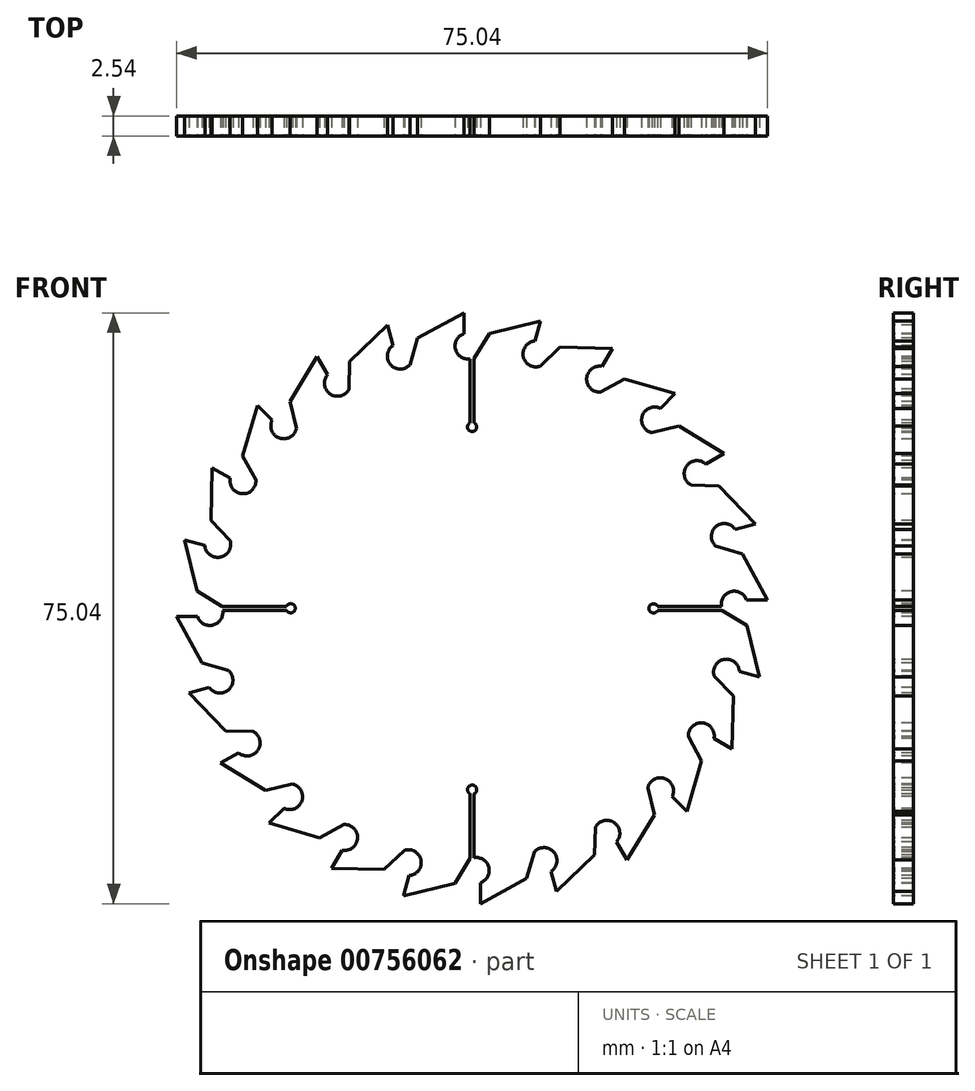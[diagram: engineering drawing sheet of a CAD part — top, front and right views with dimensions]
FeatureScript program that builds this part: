
annotation { "Feature Type Name" : "Feature", "Feature Type Description" : "" }
export const myFeature = defineFeature(function(context is Context, id is Id, definition is map)
    precondition{}
    {
        {
            var Q0;
            Q0=qCreatedBy(makeId("Front.planeOp"),FACE);
            var sketch = newSketch(context, id + "F0", { "sketchPlane" : qUnion([Q0])});
            skCircle(sketch, "E0", {"center": v(0, 0) * mm, "radius": 38.1 * mm});
            skSolve(sketch);
        }
        {
            var Q0;
            Q0 = qSketchRegion(id + "F0", true);
            extrude(context, id + "F1", {"entities" : qUnion([Q0]), "endBound" : BoundingType.SYMMETRIC, "depth" : 2.54 * mm, "offsetDistance" : 25.4 * mm});
        }
        {
            var Q0;
            Q0=makeQuery(id+"F1.opExtrude","CAP_FACE",FACE,{"disambiguationData":[OSD([sQuery(id+"F0.wireOp",EDGE,"E0")])],"isStart":false});
            var sketch = newSketch(context, id + "F2", { "sketchPlane" : qUnion([Q0])});
            skArc(sketch, "E1", {"start": v(-36.8, 9.88) * mm, "mid": v(-37.84, 4.46) * mm, "end": v(-38.09, -1.05) * mm});
            skLineSegment(sketch, "E2.bottom", {"start": v(-23.57, 0.25) * mm, "end": v(-31.75, 0.25) * mm});
            skLineSegment(sketch, "E2.top", {"start": v(-23.57, -0.25) * mm, "end": v(-31.69, -0.25) * mm});
            skArc(sketch, "E3", {"start": v(-23.57, -0.25) * mm, "mid": v(-22.46, 0) * mm, "end": v(-23.57, 0.25) * mm});
            skArc(sketch, "E4", {"start": v(-34.87, -1.05) * mm, "mid": v(-32.9, -2.12) * mm, "end": v(-31.69, -0.25) * mm});
            skLineSegment(sketch, "E5", {"start": v(-34.87, -1.05) * mm, "end": v(-38.09, -1.05) * mm});
            skLineSegment(sketch, "E6", {"start": v(-31.75, 0.25) * mm, "end": v(-34.93, 2.2) * mm});
            skLineSegment(sketch, "E7", {"start": v(-34.93, 2.2) * mm, "end": v(-36.8, 9.88) * mm});
            skLineSegment(sketch, "E8.1.0", {"start": v(0.25, -23.57) * mm, "end": v(0.25, -31.69) * mm});
            skLineSegment(sketch, "E8.1.1", {"start": v(-0.25, -23.57) * mm, "end": v(-0.25, -31.75) * mm});
            skArc(sketch, "E8.1.2", {"start": v(-9.88, -36.8) * mm, "mid": v(-4.46, -37.84) * mm, "end": v(1.05, -38.09) * mm});
            skLineSegment(sketch, "E8.1.3", {"start": v(-2.2, -34.93) * mm, "end": v(-9.88, -36.8) * mm});
            skArc(sketch, "E8.1.4", {"start": v(-9.88, -36.8) * mm, "mid": v(-4.46, -37.84) * mm, "end": v(1.05, -38.09) * mm});
            skLineSegment(sketch, "E8.1.5", {"start": v(-0.25, -31.75) * mm, "end": v(-2.2, -34.93) * mm});
            skLineSegment(sketch, "E8.1.6", {"start": v(1.05, -34.87) * mm, "end": v(1.05, -38.09) * mm});
            skArc(sketch, "E8.1.7", {"start": v(1.05, -34.87) * mm, "mid": v(2.12, -32.9) * mm, "end": v(0.25, -31.69) * mm});
            skArc(sketch, "E8.1.8", {"start": v(0.25, -23.57) * mm, "mid": v(0, -22.46) * mm, "end": v(-0.25, -23.57) * mm});
            skLineSegment(sketch, "E8.2.0", {"start": v(23.57, 0.25) * mm, "end": v(31.69, 0.25) * mm});
            skLineSegment(sketch, "E8.2.1", {"start": v(23.57, -0.25) * mm, "end": v(31.75, -0.25) * mm});
            skArc(sketch, "E8.2.2", {"start": v(36.8, -9.88) * mm, "mid": v(37.84, -4.46) * mm, "end": v(38.09, 1.05) * mm});
            skLineSegment(sketch, "E8.2.3", {"start": v(34.93, -2.2) * mm, "end": v(36.8, -9.88) * mm});
            skArc(sketch, "E8.2.4", {"start": v(36.8, -9.88) * mm, "mid": v(37.84, -4.46) * mm, "end": v(38.09, 1.05) * mm});
            skLineSegment(sketch, "E8.2.5", {"start": v(31.75, -0.25) * mm, "end": v(34.93, -2.2) * mm});
            skLineSegment(sketch, "E8.2.6", {"start": v(34.87, 1.05) * mm, "end": v(38.09, 1.05) * mm});
            skArc(sketch, "E8.2.7", {"start": v(34.87, 1.05) * mm, "mid": v(32.9, 2.12) * mm, "end": v(31.69, 0.25) * mm});
            skArc(sketch, "E8.2.8", {"start": v(23.57, 0.25) * mm, "mid": v(22.46, 0) * mm, "end": v(23.57, -0.25) * mm});
            skLineSegment(sketch, "E8.3.0", {"start": v(-0.25, 23.57) * mm, "end": v(-0.25, 31.69) * mm});
            skLineSegment(sketch, "E8.3.1", {"start": v(0.25, 23.57) * mm, "end": v(0.25, 31.75) * mm});
            skArc(sketch, "E8.3.2", {"start": v(9.88, 36.8) * mm, "mid": v(4.46, 37.84) * mm, "end": v(-1.05, 38.09) * mm});
            skLineSegment(sketch, "E8.3.3", {"start": v(2.2, 34.93) * mm, "end": v(9.88, 36.8) * mm});
            skArc(sketch, "E8.3.4", {"start": v(9.88, 36.8) * mm, "mid": v(4.46, 37.84) * mm, "end": v(-1.05, 38.09) * mm});
            skLineSegment(sketch, "E8.3.5", {"start": v(0.25, 31.75) * mm, "end": v(2.2, 34.93) * mm});
            skLineSegment(sketch, "E8.3.6", {"start": v(-1.05, 34.87) * mm, "end": v(-1.05, 38.09) * mm});
            skArc(sketch, "E8.3.7", {"start": v(-1.05, 34.87) * mm, "mid": v(-2.12, 32.9) * mm, "end": v(-0.25, 31.69) * mm});
            skArc(sketch, "E8.3.8", {"start": v(-0.25, 23.57) * mm, "mid": v(0, 22.46) * mm, "end": v(0.25, 23.57) * mm});
            skSolve(sketch);
        }
        {
            var Q0;
            Q0 = qSketchRegion(id + "F2", true);
            var Q1;
            Q1=makeQuery(id+"F1.opExtrude","CAP_FACE",FACE,{"disambiguationData":[OSD([sQuery(id+"F0.wireOp",EDGE,"E0")])],"isStart":true});
            extrude(context, id + "F3", {"entities" : qUnion([Q0]), "operationType" : NewBodyOperationType.REMOVE, "endBound" : BoundingType.UP_TO_SURFACE, "oppositeDirection" : true, "depth" : 25.4 * mm, "endBoundEntityFace" : qUnion([Q1]), "offsetDistance" : 25.4 * mm});
        }
        {
            var Q0;
            Q0=makeQuery(id+"F1.opExtrude","CAP_FACE",FACE,{"disambiguationData":[OSD([sQuery(id+"F0.wireOp",EDGE,"E0")])],"isStart":false});
            var sketch = newSketch(context, id + "F4", { "sketchPlane" : qUnion([Q0])});
            skLineSegment(sketch, "E9", {"start": v(-36.8, 9.88) * mm, "end": v(-34.93, 2.2) * mm});
            skArc(sketch, "E10", {"start": v(-34.87, -1.05) * mm, "mid": v(-32.6, -2.01) * mm, "end": v(-31.92, 0.36) * mm});
            skLineSegment(sketch, "E11", {"start": v(-34.93, 2.2) * mm, "end": v(-31.92, 0.36) * mm});
            skLineSegment(sketch, "E12", {"start": v(-34.87, -1.05) * mm, "end": v(-38.09, -1.05) * mm});
            skArc(sketch, "E13", {"start": v(-36.8, 9.88) * mm, "mid": v(-37.84, 4.46) * mm, "end": v(-38.09, -1.05) * mm});
            skPoint(sketch, "E13.third.point", {"position": v(35.39, -14.11) * mm});
            skArc(sketch, "E14.1.0", {"start": v(-38.1, 0.02) * mm, "mid": v(-37.7, -5.49) * mm, "end": v(-36.52, -10.87) * mm});
            skLineSegment(sketch, "E14.1.1", {"start": v(-34.31, -6.92) * mm, "end": v(-30.93, -7.91) * mm});
            skLineSegment(sketch, "E14.1.2", {"start": v(-33.41, -10.04) * mm, "end": v(-36.52, -10.87) * mm});
            skLineSegment(sketch, "E14.1.3", {"start": v(-38.1, 0.02) * mm, "end": v(-34.31, -6.92) * mm});
            skArc(sketch, "E14.1.4", {"start": v(-33.41, -10.04) * mm, "mid": v(-30.97, -10.38) * mm, "end": v(-30.93, -7.91) * mm});
            skArc(sketch, "E14.2.0", {"start": v(-36.8, -9.85) * mm, "mid": v(-35, -15.06) * mm, "end": v(-32.46, -19.96) * mm});
            skLineSegment(sketch, "E14.2.1", {"start": v(-31.35, -15.57) * mm, "end": v(-27.83, -15.65) * mm});
            skLineSegment(sketch, "E14.2.2", {"start": v(-29.67, -18.35) * mm, "end": v(-32.46, -19.96) * mm});
            skLineSegment(sketch, "E14.2.3", {"start": v(-36.8, -9.85) * mm, "end": v(-31.35, -15.57) * mm});
            skArc(sketch, "E14.2.4", {"start": v(-29.67, -18.35) * mm, "mid": v(-27.22, -18.04) * mm, "end": v(-27.83, -15.65) * mm});
            skArc(sketch, "E14.3.0", {"start": v(-33, -19.04) * mm, "mid": v(-29.9, -23.6) * mm, "end": v(-26.19, -27.68) * mm});
            skLineSegment(sketch, "E14.3.1", {"start": v(-26.25, -23.15) * mm, "end": v(-22.83, -22.32) * mm});
            skLineSegment(sketch, "E14.3.2", {"start": v(-23.91, -25.4) * mm, "end": v(-26.19, -27.68) * mm});
            skLineSegment(sketch, "E14.3.3", {"start": v(-33, -19.04) * mm, "end": v(-26.25, -23.15) * mm});
            skArc(sketch, "E14.3.4", {"start": v(-23.91, -25.4) * mm, "mid": v(-21.63, -24.47) * mm, "end": v(-22.83, -22.32) * mm});
            skArc(sketch, "E14.4.0", {"start": v(-26.95, -26.93) * mm, "mid": v(-22.78, -30.54) * mm, "end": v(-18.13, -33.5) * mm});
            skLineSegment(sketch, "E14.4.1", {"start": v(-19.37, -29.16) * mm, "end": v(-16.27, -27.47) * mm});
            skLineSegment(sketch, "E14.4.2", {"start": v(-16.52, -30.73) * mm, "end": v(-18.13, -33.5) * mm});
            skLineSegment(sketch, "E14.4.3", {"start": v(-26.95, -26.93) * mm, "end": v(-19.37, -29.16) * mm});
            skArc(sketch, "E14.4.4", {"start": v(-16.52, -30.73) * mm, "mid": v(-14.56, -29.24) * mm, "end": v(-16.27, -27.47) * mm});
            skArc(sketch, "E14.5.0", {"start": v(-19.06, -32.99) * mm, "mid": v(-14.1, -35.4) * mm, "end": v(-8.84, -37.06) * mm});
            skLineSegment(sketch, "E14.5.1", {"start": v(-11.16, -33.17) * mm, "end": v(-8.61, -30.74) * mm});
            skLineSegment(sketch, "E14.5.2", {"start": v(-8, -33.96) * mm, "end": v(-8.84, -37.06) * mm});
            skLineSegment(sketch, "E14.5.3", {"start": v(-19.06, -32.99) * mm, "end": v(-11.16, -33.17) * mm});
            skArc(sketch, "E14.5.4", {"start": v(-8, -33.96) * mm, "mid": v(-6.5, -32) * mm, "end": v(-8.61, -30.74) * mm});
            skArc(sketch, "E14.6.0", {"start": v(-9.88, -36.8) * mm, "mid": v(-4.46, -37.84) * mm, "end": v(1.05, -38.09) * mm});
            skLineSegment(sketch, "E14.6.1", {"start": v(-2.2, -34.93) * mm, "end": v(-0.36, -31.92) * mm});
            skLineSegment(sketch, "E14.6.2", {"start": v(1.05, -34.87) * mm, "end": v(1.05, -38.09) * mm});
            skLineSegment(sketch, "E14.6.3", {"start": v(-9.88, -36.8) * mm, "end": v(-2.2, -34.93) * mm});
            skArc(sketch, "E14.6.4", {"start": v(1.05, -34.87) * mm, "mid": v(2.01, -32.6) * mm, "end": v(-0.36, -31.92) * mm});
            skArc(sketch, "E14.7.0", {"start": v(-0.02, -38.1) * mm, "mid": v(5.49, -37.7) * mm, "end": v(10.87, -36.52) * mm});
            skLineSegment(sketch, "E14.7.1", {"start": v(6.92, -34.31) * mm, "end": v(7.91, -30.93) * mm});
            skLineSegment(sketch, "E14.7.2", {"start": v(10.04, -33.41) * mm, "end": v(10.87, -36.52) * mm});
            skLineSegment(sketch, "E14.7.3", {"start": v(-0.02, -38.1) * mm, "end": v(6.92, -34.31) * mm});
            skArc(sketch, "E14.7.4", {"start": v(10.04, -33.41) * mm, "mid": v(10.38, -30.97) * mm, "end": v(7.91, -30.93) * mm});
            skArc(sketch, "E14.8.0", {"start": v(9.85, -36.8) * mm, "mid": v(15.06, -35) * mm, "end": v(19.96, -32.46) * mm});
            skLineSegment(sketch, "E14.8.1", {"start": v(15.57, -31.35) * mm, "end": v(15.65, -27.83) * mm});
            skLineSegment(sketch, "E14.8.2", {"start": v(18.35, -29.67) * mm, "end": v(19.96, -32.46) * mm});
            skLineSegment(sketch, "E14.8.3", {"start": v(9.85, -36.8) * mm, "end": v(15.57, -31.35) * mm});
            skArc(sketch, "E14.8.4", {"start": v(18.35, -29.67) * mm, "mid": v(18.04, -27.22) * mm, "end": v(15.65, -27.83) * mm});
            skArc(sketch, "E14.9.0", {"start": v(19.04, -33) * mm, "mid": v(23.6, -29.9) * mm, "end": v(27.68, -26.19) * mm});
            skLineSegment(sketch, "E14.9.1", {"start": v(23.15, -26.25) * mm, "end": v(22.32, -22.83) * mm});
            skLineSegment(sketch, "E14.9.2", {"start": v(25.4, -23.91) * mm, "end": v(27.68, -26.19) * mm});
            skLineSegment(sketch, "E14.9.3", {"start": v(19.04, -33) * mm, "end": v(23.15, -26.25) * mm});
            skArc(sketch, "E14.9.4", {"start": v(25.4, -23.91) * mm, "mid": v(24.47, -21.63) * mm, "end": v(22.32, -22.83) * mm});
            skArc(sketch, "E14.10.0", {"start": v(26.93, -26.95) * mm, "mid": v(30.54, -22.78) * mm, "end": v(33.5, -18.13) * mm});
            skLineSegment(sketch, "E14.10.1", {"start": v(29.16, -19.37) * mm, "end": v(27.47, -16.27) * mm});
            skLineSegment(sketch, "E14.10.2", {"start": v(30.73, -16.52) * mm, "end": v(33.5, -18.13) * mm});
            skLineSegment(sketch, "E14.10.3", {"start": v(26.93, -26.95) * mm, "end": v(29.16, -19.37) * mm});
            skArc(sketch, "E14.10.4", {"start": v(30.73, -16.52) * mm, "mid": v(29.24, -14.56) * mm, "end": v(27.47, -16.27) * mm});
            skArc(sketch, "E14.11.0", {"start": v(32.99, -19.06) * mm, "mid": v(35.4, -14.1) * mm, "end": v(37.06, -8.84) * mm});
            skLineSegment(sketch, "E14.11.1", {"start": v(33.17, -11.16) * mm, "end": v(30.74, -8.61) * mm});
            skLineSegment(sketch, "E14.11.2", {"start": v(33.96, -8) * mm, "end": v(37.06, -8.84) * mm});
            skLineSegment(sketch, "E14.11.3", {"start": v(32.99, -19.06) * mm, "end": v(33.17, -11.16) * mm});
            skArc(sketch, "E14.11.4", {"start": v(33.96, -8) * mm, "mid": v(32, -6.5) * mm, "end": v(30.74, -8.61) * mm});
            skArc(sketch, "E14.12.0", {"start": v(36.8, -9.88) * mm, "mid": v(37.84, -4.46) * mm, "end": v(38.09, 1.05) * mm});
            skLineSegment(sketch, "E14.12.1", {"start": v(34.93, -2.2) * mm, "end": v(31.92, -0.36) * mm});
            skLineSegment(sketch, "E14.12.2", {"start": v(34.87, 1.05) * mm, "end": v(38.09, 1.05) * mm});
            skLineSegment(sketch, "E14.12.3", {"start": v(36.8, -9.88) * mm, "end": v(34.93, -2.2) * mm});
            skArc(sketch, "E14.12.4", {"start": v(34.87, 1.05) * mm, "mid": v(32.6, 2.01) * mm, "end": v(31.92, -0.36) * mm});
            skArc(sketch, "E14.13.0", {"start": v(38.1, -0.02) * mm, "mid": v(37.7, 5.49) * mm, "end": v(36.52, 10.87) * mm});
            skLineSegment(sketch, "E14.13.1", {"start": v(34.31, 6.92) * mm, "end": v(30.93, 7.91) * mm});
            skLineSegment(sketch, "E14.13.2", {"start": v(33.41, 10.04) * mm, "end": v(36.52, 10.87) * mm});
            skLineSegment(sketch, "E14.13.3", {"start": v(38.1, -0.02) * mm, "end": v(34.31, 6.92) * mm});
            skArc(sketch, "E14.13.4", {"start": v(33.41, 10.04) * mm, "mid": v(30.97, 10.38) * mm, "end": v(30.93, 7.91) * mm});
            skArc(sketch, "E14.14.0", {"start": v(36.8, 9.85) * mm, "mid": v(35, 15.06) * mm, "end": v(32.46, 19.96) * mm});
            skLineSegment(sketch, "E14.14.1", {"start": v(31.35, 15.57) * mm, "end": v(27.83, 15.65) * mm});
            skLineSegment(sketch, "E14.14.2", {"start": v(29.67, 18.35) * mm, "end": v(32.46, 19.96) * mm});
            skLineSegment(sketch, "E14.14.3", {"start": v(36.8, 9.85) * mm, "end": v(31.35, 15.57) * mm});
            skArc(sketch, "E14.14.4", {"start": v(29.67, 18.35) * mm, "mid": v(27.22, 18.04) * mm, "end": v(27.83, 15.65) * mm});
            skArc(sketch, "E14.15.0", {"start": v(33, 19.04) * mm, "mid": v(29.9, 23.6) * mm, "end": v(26.19, 27.68) * mm});
            skLineSegment(sketch, "E14.15.1", {"start": v(26.25, 23.15) * mm, "end": v(22.83, 22.32) * mm});
            skLineSegment(sketch, "E14.15.2", {"start": v(23.91, 25.4) * mm, "end": v(26.19, 27.68) * mm});
            skLineSegment(sketch, "E14.15.3", {"start": v(33, 19.04) * mm, "end": v(26.25, 23.15) * mm});
            skArc(sketch, "E14.15.4", {"start": v(23.91, 25.4) * mm, "mid": v(21.63, 24.47) * mm, "end": v(22.83, 22.32) * mm});
            skArc(sketch, "E14.16.0", {"start": v(26.95, 26.93) * mm, "mid": v(22.78, 30.54) * mm, "end": v(18.13, 33.5) * mm});
            skLineSegment(sketch, "E14.16.1", {"start": v(19.37, 29.16) * mm, "end": v(16.27, 27.47) * mm});
            skLineSegment(sketch, "E14.16.2", {"start": v(16.52, 30.73) * mm, "end": v(18.13, 33.5) * mm});
            skLineSegment(sketch, "E14.16.3", {"start": v(26.95, 26.93) * mm, "end": v(19.37, 29.16) * mm});
            skArc(sketch, "E14.16.4", {"start": v(16.52, 30.73) * mm, "mid": v(14.56, 29.24) * mm, "end": v(16.27, 27.47) * mm});
            skArc(sketch, "E14.17.0", {"start": v(19.06, 32.99) * mm, "mid": v(14.1, 35.4) * mm, "end": v(8.84, 37.06) * mm});
            skLineSegment(sketch, "E14.17.1", {"start": v(11.16, 33.17) * mm, "end": v(8.61, 30.74) * mm});
            skLineSegment(sketch, "E14.17.2", {"start": v(8, 33.96) * mm, "end": v(8.84, 37.06) * mm});
            skLineSegment(sketch, "E14.17.3", {"start": v(19.06, 32.99) * mm, "end": v(11.16, 33.17) * mm});
            skArc(sketch, "E14.17.4", {"start": v(8, 33.96) * mm, "mid": v(6.5, 32) * mm, "end": v(8.61, 30.74) * mm});
            skArc(sketch, "E14.18.0", {"start": v(9.88, 36.8) * mm, "mid": v(4.46, 37.84) * mm, "end": v(-1.05, 38.09) * mm});
            skLineSegment(sketch, "E14.18.1", {"start": v(2.2, 34.93) * mm, "end": v(0.36, 31.92) * mm});
            skLineSegment(sketch, "E14.18.2", {"start": v(-1.05, 34.87) * mm, "end": v(-1.05, 38.09) * mm});
            skLineSegment(sketch, "E14.18.3", {"start": v(9.88, 36.8) * mm, "end": v(2.2, 34.93) * mm});
            skArc(sketch, "E14.18.4", {"start": v(-1.05, 34.87) * mm, "mid": v(-2.01, 32.6) * mm, "end": v(0.36, 31.92) * mm});
            skArc(sketch, "E14.19.0", {"start": v(0.02, 38.1) * mm, "mid": v(-5.49, 37.7) * mm, "end": v(-10.87, 36.52) * mm});
            skLineSegment(sketch, "E14.19.1", {"start": v(-6.92, 34.31) * mm, "end": v(-7.91, 30.93) * mm});
            skLineSegment(sketch, "E14.19.2", {"start": v(-10.04, 33.41) * mm, "end": v(-10.87, 36.52) * mm});
            skLineSegment(sketch, "E14.19.3", {"start": v(0.02, 38.1) * mm, "end": v(-6.92, 34.31) * mm});
            skArc(sketch, "E14.19.4", {"start": v(-10.04, 33.41) * mm, "mid": v(-10.38, 30.97) * mm, "end": v(-7.91, 30.93) * mm});
            skArc(sketch, "E14.20.0", {"start": v(-9.85, 36.8) * mm, "mid": v(-15.06, 35) * mm, "end": v(-19.96, 32.46) * mm});
            skLineSegment(sketch, "E14.20.1", {"start": v(-15.57, 31.35) * mm, "end": v(-15.65, 27.83) * mm});
            skLineSegment(sketch, "E14.20.2", {"start": v(-18.35, 29.67) * mm, "end": v(-19.96, 32.46) * mm});
            skLineSegment(sketch, "E14.20.3", {"start": v(-9.85, 36.8) * mm, "end": v(-15.57, 31.35) * mm});
            skArc(sketch, "E14.20.4", {"start": v(-18.35, 29.67) * mm, "mid": v(-18.04, 27.22) * mm, "end": v(-15.65, 27.83) * mm});
            skArc(sketch, "E14.21.0", {"start": v(-19.04, 33) * mm, "mid": v(-23.6, 29.9) * mm, "end": v(-27.68, 26.19) * mm});
            skLineSegment(sketch, "E14.21.1", {"start": v(-23.15, 26.25) * mm, "end": v(-22.32, 22.83) * mm});
            skLineSegment(sketch, "E14.21.2", {"start": v(-25.4, 23.91) * mm, "end": v(-27.68, 26.19) * mm});
            skLineSegment(sketch, "E14.21.3", {"start": v(-19.04, 33) * mm, "end": v(-23.15, 26.25) * mm});
            skArc(sketch, "E14.21.4", {"start": v(-25.4, 23.91) * mm, "mid": v(-24.47, 21.63) * mm, "end": v(-22.32, 22.83) * mm});
            skArc(sketch, "E14.22.0", {"start": v(-26.93, 26.95) * mm, "mid": v(-30.54, 22.78) * mm, "end": v(-33.5, 18.13) * mm});
            skLineSegment(sketch, "E14.22.1", {"start": v(-29.16, 19.37) * mm, "end": v(-27.47, 16.27) * mm});
            skLineSegment(sketch, "E14.22.2", {"start": v(-30.73, 16.52) * mm, "end": v(-33.5, 18.13) * mm});
            skLineSegment(sketch, "E14.22.3", {"start": v(-26.93, 26.95) * mm, "end": v(-29.16, 19.37) * mm});
            skArc(sketch, "E14.22.4", {"start": v(-30.73, 16.52) * mm, "mid": v(-29.24, 14.56) * mm, "end": v(-27.47, 16.27) * mm});
            skArc(sketch, "E14.23.0", {"start": v(-32.99, 19.06) * mm, "mid": v(-35.4, 14.1) * mm, "end": v(-37.06, 8.84) * mm});
            skLineSegment(sketch, "E14.23.1", {"start": v(-33.17, 11.16) * mm, "end": v(-30.74, 8.61) * mm});
            skLineSegment(sketch, "E14.23.2", {"start": v(-33.96, 8) * mm, "end": v(-37.06, 8.84) * mm});
            skLineSegment(sketch, "E14.23.3", {"start": v(-32.99, 19.06) * mm, "end": v(-33.17, 11.16) * mm});
            skArc(sketch, "E14.23.4", {"start": v(-33.96, 8) * mm, "mid": v(-32, 6.5) * mm, "end": v(-30.74, 8.61) * mm});
            skSolve(sketch);
        }
        {
            var Q0;
            Q0 = qSketchRegion(id + "F4", true);
            var Q1;
            Q1=makeQuery(id+"F1.opExtrude","CAP_FACE",FACE,{"disambiguationData":[OSD([sQuery(id+"F0.wireOp",EDGE,"E0")])],"isStart":true});
            var Q2;
            Q2=makeQuery(id+"F1.opExtrude","CAP_FACE",FACE,{"disambiguationData":[OSD([sQuery(id+"F0.wireOp",EDGE,"E0")])],"isStart":true});
            extrude(context, id + "F5", {"entities" : qUnion([Q0, Q1]), "operationType" : NewBodyOperationType.REMOVE, "endBound" : BoundingType.THROUGH_ALL, "oppositeDirection" : true, "depth" : 25.4 * mm, "endBoundEntityFace" : qUnion([Q2]), "offsetDistance" : 25.4 * mm});
        }
    });
